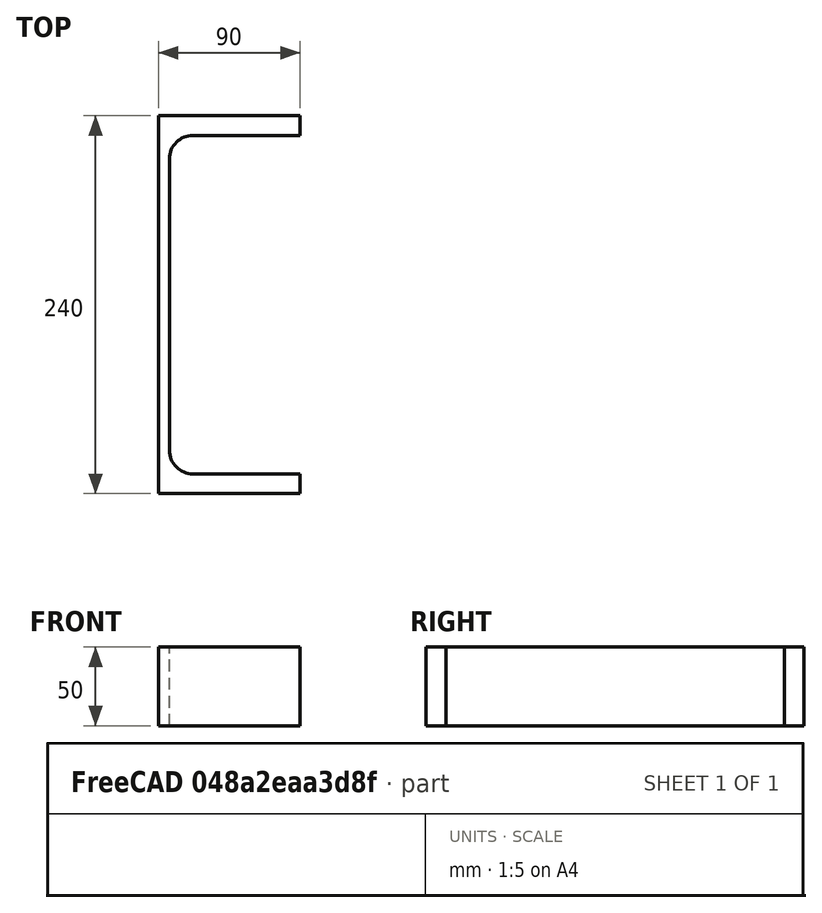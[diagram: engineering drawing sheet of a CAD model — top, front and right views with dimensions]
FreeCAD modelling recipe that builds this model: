
FCSTD DOCUMENT  (FreeCAD 0.20R29410 (Git))
Label: UPE-Profile 240 DIN1026-2 S235JR
License: All rights reserved
LicenseURL: http://en.wikipedia.org/wiki/All_rights_reserved
objects: Sketcher::SketchObject×1, Part::Extrusion×1
note: 2 computed .brp shape members not serialized (recipe doc carries the construction recipe); baked Part::Feature solids carry a one-line shape summary decoded from their .brp

FEATURE [Sketcher::SketchObject] Sketch
  FullyConstrained = true
  MapMode = 5
  sketch-geometry (10):
    g0: LineSegment StartX=7 StartY=-92.5 StartZ=0 EndX=7 EndY=92.5 EndZ=0
    g1: LineSegment StartX=22 StartY=107.5 StartZ=0 EndX=90 EndY=107.5 EndZ=0
    g2: LineSegment StartX=90 StartY=107.5 StartZ=0 EndX=90 EndY=120 EndZ=0
    g3: LineSegment StartX=90 StartY=-120 StartZ=0 EndX=90 EndY=-107.5 EndZ=0
    g4: LineSegment StartX=90 StartY=-107.5 StartZ=0 EndX=22 EndY=-107.5 EndZ=0
    g5: ArcOfCircle CenterX=22 CenterY=92.5 CenterZ=0 NormalX=0 NormalY=0 NormalZ=1 AngleXU=0 Radius=15 StartAngle=1.5708 EndAngle=3.14159
    g6: ArcOfCircle CenterX=22 CenterY=-92.5 CenterZ=0 NormalX=0 NormalY=0 NormalZ=1 AngleXU=0 Radius=15 StartAngle=3.14159 EndAngle=4.71239
    g7: LineSegment StartX=90 StartY=-120 StartZ=0 EndX=0 EndY=-120 EndZ=0
    g8: LineSegment StartX=0 StartY=-120 StartZ=0 EndX=0 EndY=120 EndZ=0
    g9: LineSegment StartX=0 StartY=120 StartZ=0 EndX=90 EndY=120 EndZ=0
  constraints (27):
    c: Vertical(g0)
    c: Coincident(g2,g1)
    c: Vertical(g2)
    c: Vertical(g3)
    c: Coincident(g4,g3)
    c: Horizontal(g4)
    c: Tangent(g1,g5) = 1.5708
    c: Tangent(g0,g5) = 1.5708
    c: Tangent(g0,g6) = 1.5708
    c: Tangent(g4,g6) = 1.5708
    c: Symmetric(g2,g3,g-1)
    c: DistanceY(g2) = 12.5
    c: Radius(g5) = 15
    c: Coincident(g3,g7)
    c: PointOnObject(g7,g-2)
    c: Horizontal(g7)
    c: Coincident(g7,g8)
    c: PointOnObject(g8,g-2)
    c: Coincident(g8,g9)
    c: Coincident(g9,g2)
    c: Horizontal(g9)
    c: Distance(g-1,g0) = 7
    c: DistanceX(g9,g9) = 90
    c: Horizontal(g1)
    c: Equal(g3,g2)
    c: Equal(g5,g6)
    c: DistanceY(g3,g2) = 240
FEATURE [Part::Extrusion] Extrude  label="UPE-Profile 240 DIN1026-2 S235JR"
  Base = -> Sketch
  Dir = (0,0,50)
  DirMode = 0
  FaceMakerClass = Part::FaceMakerExtrusion
  LengthFwd = 0
  LengthRev = 0
  Solid = true
  Symmetric = false
